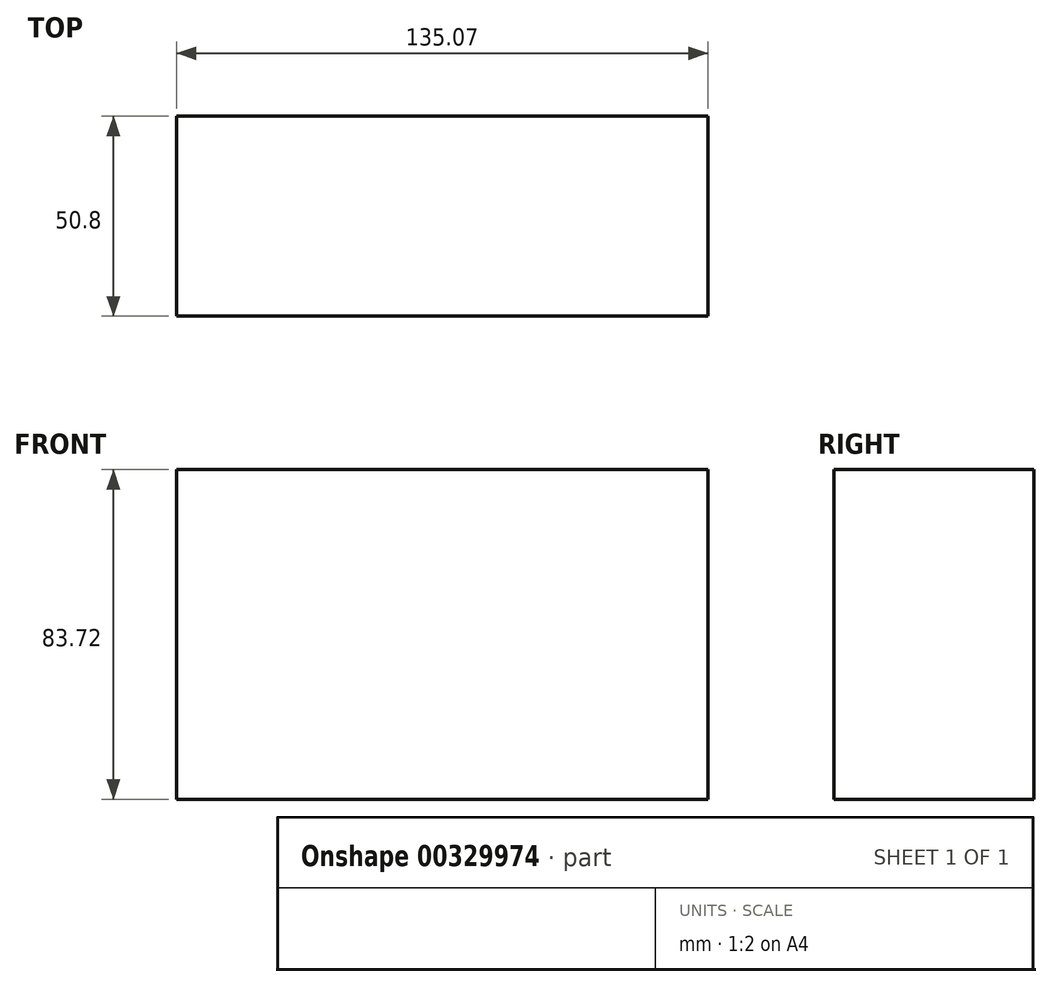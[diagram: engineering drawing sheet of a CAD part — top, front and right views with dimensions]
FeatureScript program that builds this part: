
annotation { "Feature Type Name" : "Feature", "Feature Type Description" : "" }
export const myFeature = defineFeature(function(context is Context, id is Id, definition is map)
    precondition{}
    {
        {
            var Q0;
            Q0=qCreatedBy(makeId("Front.planeOp"),FACE);
            var sketch = newSketch(context, id + "F0", { "sketchPlane" : qUnion([Q0])});
            skLineSegment(sketch, "E0", {"start": v(-126.47, 51.8) * mm, "end": v(-126.47, -31.9) * mm});
            skLineSegment(sketch, "E1", {"start": v(-126.47, -31.9) * mm, "end": v(8.6, -31.9) * mm});
            skLineSegment(sketch, "E2", {"start": v(8.6, -31.9) * mm, "end": v(8.6, 51.8) * mm});
            skLineSegment(sketch, "E3", {"start": v(8.6, 51.8) * mm, "end": v(-126.47, 51.8) * mm});
            skSolve(sketch);
        }
        {
            var Q0;
            Q0 = qSketchRegion(id + "F0", true);
            extrude(context, id + "F1", {"entities" : qUnion([Q0]), "depth" : 50.8 * mm});
        }
    });
